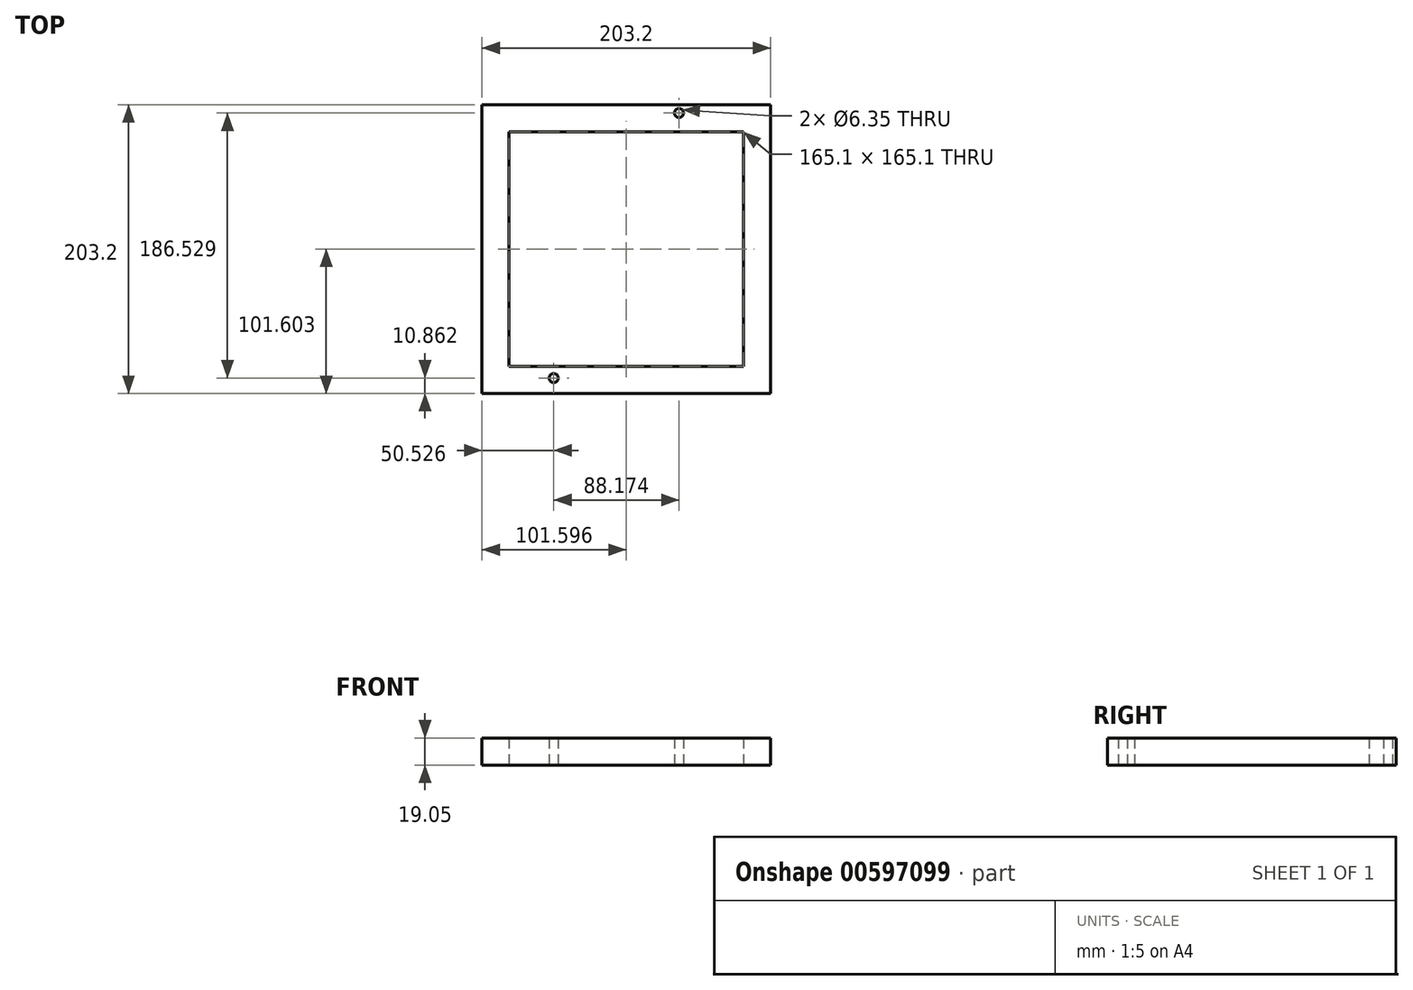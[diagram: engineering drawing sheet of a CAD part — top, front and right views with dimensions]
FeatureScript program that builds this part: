
annotation { "Feature Type Name" : "Feature", "Feature Type Description" : "" }
export const myFeature = defineFeature(function(context is Context, id is Id, definition is map)
    precondition{}
    {
        {
            var Q0;
            Q0=qCreatedBy(makeId("Top.planeOp"),FACE);
            var sketch = newSketch(context, id + "F0", { "sketchPlane" : qUnion([Q0])});
            skLineSegment(sketch, "E0.bottom", {"start": v(-138.7, 143.63) * mm, "end": v(64.5, 143.63) * mm});
            skLineSegment(sketch, "E0.top", {"start": v(-138.7, -59.57) * mm, "end": v(64.5, -59.57) * mm});
            skLineSegment(sketch, "E0.left", {"start": v(-138.7, 143.63) * mm, "end": v(-138.7, -59.57) * mm});
            skLineSegment(sketch, "E0.right", {"start": v(64.5, 143.63) * mm, "end": v(64.5, -59.57) * mm});
            skLineSegment(sketch, "E1.0", {"start": v(-119.65, 124.58) * mm, "end": v(45.45, 124.58) * mm});
            skLineSegment(sketch, "E1.1", {"start": v(-119.65, 124.58) * mm, "end": v(-119.65, -40.52) * mm});
            skLineSegment(sketch, "E1.2", {"start": v(-119.65, -40.52) * mm, "end": v(45.45, -40.52) * mm});
            skLineSegment(sketch, "E1.3", {"start": v(45.45, 124.58) * mm, "end": v(45.45, -40.52) * mm});
            skCircle(sketch, "E2", {"center": v(0, 137.82) * mm, "radius": 3.18 * mm});
            skCircle(sketch, "E3", {"center": v(-88.17, -48.7) * mm, "radius": 3.18 * mm});
            skSolve(sketch);
        }
        {
            var Q0;
            Q0=makeQuery(id+"F0.imprint","IMPRINT",FACE,{"disambiguationData":[TD([[makeQuery(id+"F0.imprint","IMPRINT",EDGE,{"derivedFrom":sQuery(id+"F0.wireOp",EDGE,"E0.bottom")}),-1.0]])]});
            extrude(context, id + "F1", {"entities" : qUnion([Q0]), "depth" : 19.05 * mm, "offsetDistance" : 25.4 * mm});
        }
    });
